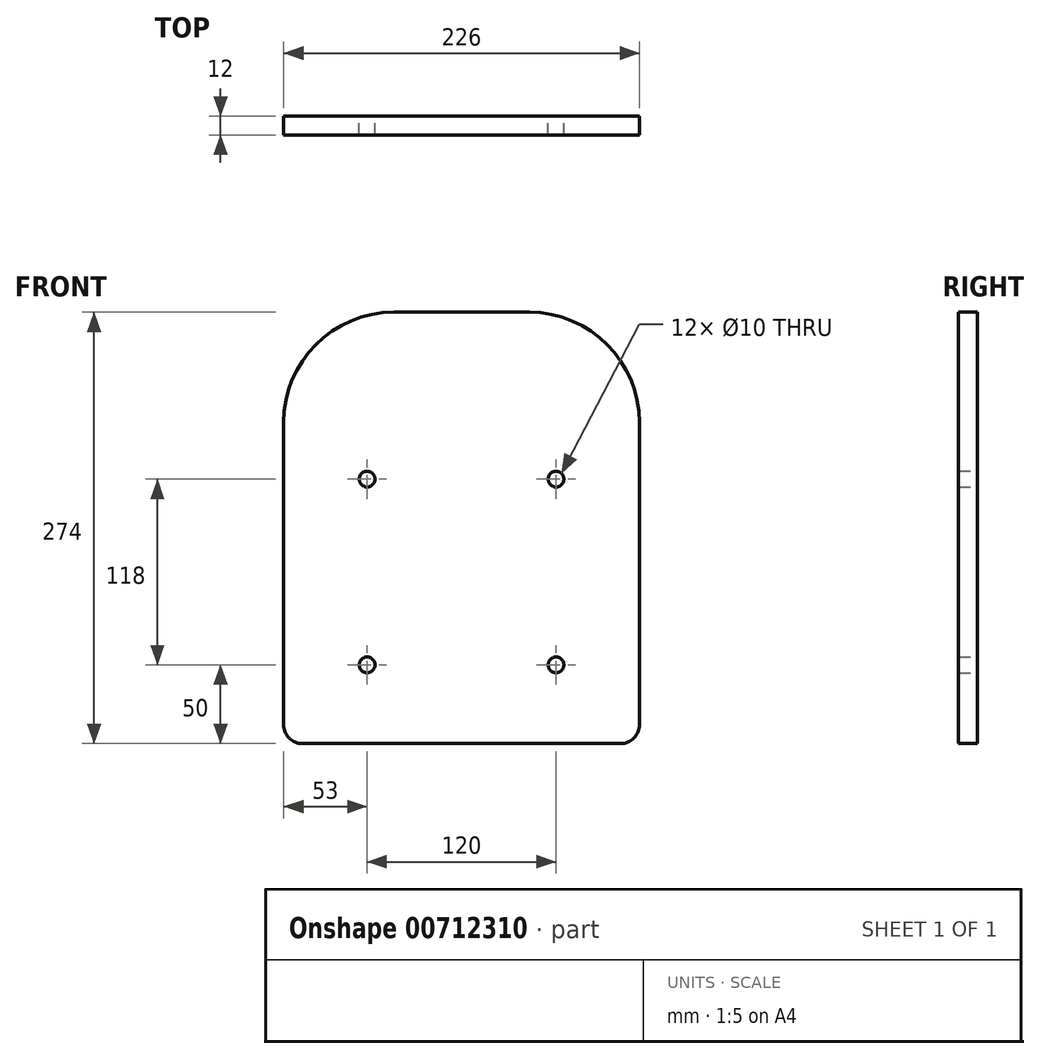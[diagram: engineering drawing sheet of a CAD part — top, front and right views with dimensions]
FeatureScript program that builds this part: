
annotation { "Feature Type Name" : "Feature", "Feature Type Description" : "" }
export const myFeature = defineFeature(function(context is Context, id is Id, definition is map)
    precondition{}
    {
        {
            var Q0;
            Q0=qCreatedBy(makeId("Front.planeOp"),FACE);
            var sketch = newSketch(context, id + "F0", { "sketchPlane" : qUnion([Q0])});
            skLineSegment(sketch, "E0.bottom", {"start": v(60, -59) * mm, "end": v(-60, -59) * mm, "construction": true});
            skLineSegment(sketch, "E0.top", {"start": v(60, 59) * mm, "end": v(-60, 59) * mm, "construction": true});
            skLineSegment(sketch, "E0.left", {"start": v(60, -59) * mm, "end": v(60, 59) * mm, "construction": true});
            skLineSegment(sketch, "E0.right", {"start": v(-60, -59) * mm, "end": v(-60, 59) * mm, "construction": true});
            skPoint(sketch, "E0.middle", {"position": v(0, 0) * mm});
            skLineSegment(sketch, "E1.bottom", {"start": v(101, -109) * mm, "end": v(-101, -109) * mm});
            skLineSegment(sketch, "E1.top", {"start": v(43, 165) * mm, "end": v(-43, 165) * mm});
            skLineSegment(sketch, "E1.left", {"start": v(113, -97) * mm, "end": v(113, 95) * mm});
            skLineSegment(sketch, "E1.right", {"start": v(-113, -97) * mm, "end": v(-113, 95) * mm});
            skPoint(sketch, "E1.middle", {"position": v(0, 28) * mm});
            skPoint(sketch, "E2.visualSharp", {"position": v(-113, 165) * mm});
            skArc(sketch, "E2.filletArc", {"start": v(-43, 165) * mm, "mid": v(-92.5, 144.5) * mm, "end": v(-113, 95) * mm});
            skPoint(sketch, "E3.visualSharp", {"position": v(113, 165) * mm});
            skArc(sketch, "E3.filletArc", {"start": v(113, 95) * mm, "mid": v(92.5, 144.5) * mm, "end": v(43, 165) * mm});
            skCircle(sketch, "E4", {"center": v(-60, 59) * mm, "radius": 5 * mm});
            skCircle(sketch, "E5", {"center": v(60, 59) * mm, "radius": 5 * mm});
            skCircle(sketch, "E6", {"center": v(60, -59) * mm, "radius": 5 * mm});
            skCircle(sketch, "E7", {"center": v(-60, -59) * mm, "radius": 5 * mm});
            skPoint(sketch, "E8.visualSharp", {"position": v(-113, -109) * mm});
            skArc(sketch, "E8.filletArc", {"start": v(-113, -97) * mm, "mid": v(-109.49, -105.49) * mm, "end": v(-101, -109) * mm});
            skPoint(sketch, "E9.visualSharp", {"position": v(113, -109) * mm});
            skArc(sketch, "E9.filletArc", {"start": v(101, -109) * mm, "mid": v(109.49, -105.49) * mm, "end": v(113, -97) * mm});
            skSolve(sketch);
        }
        {
            var Q0;
            Q0 = qSketchRegion(id + "F0", true);
            extrude(context, id + "F1", {"entities" : qUnion([Q0]), "depth" : 12 * mm, "offsetDistance" : 25 * mm});
        }
    });
